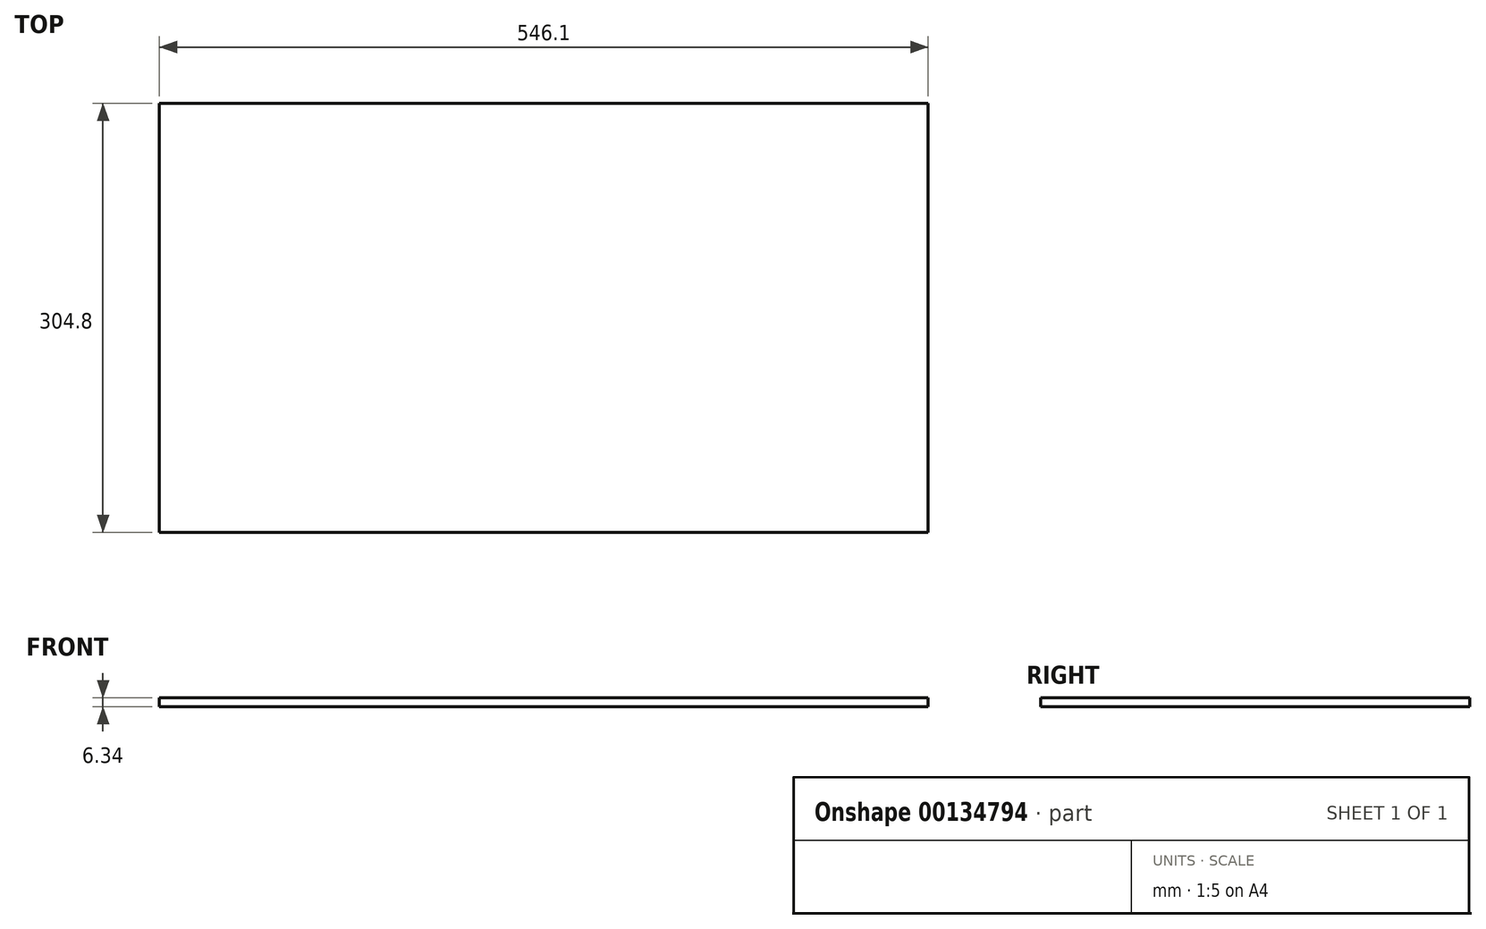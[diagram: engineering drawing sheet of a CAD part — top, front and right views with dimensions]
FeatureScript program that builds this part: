
annotation { "Feature Type Name" : "Feature", "Feature Type Description" : "" }
export const myFeature = defineFeature(function(context is Context, id is Id, definition is map)
    precondition{}
    {
        {
            var Q0;
            Q0=qCreatedBy(makeId("Top.planeOp"),FACE);
            var sketch = newSketch(context, id + "F0", { "sketchPlane" : qUnion([Q0])});
            skLineSegment(sketch, "E0.bottom", {"start": v(273.05, 152.4) * mm, "end": v(-273.05, 152.4) * mm});
            skLineSegment(sketch, "E0.top", {"start": v(273.05, -152.4) * mm, "end": v(-273.05, -152.4) * mm});
            skLineSegment(sketch, "E0.left", {"start": v(273.05, 152.4) * mm, "end": v(273.05, -152.4) * mm});
            skLineSegment(sketch, "E0.right", {"start": v(-273.05, 152.4) * mm, "end": v(-273.05, -152.4) * mm});
            skPoint(sketch, "E0.middle", {"position": v(0, 0) * mm});
            skSolve(sketch);
        }
        {
            var Q0;
            Q0=makeQuery(id+"F0.imprint","IMPRINT",FACE,{"disambiguationData":[TD([[makeQuery(id+"F0.imprint","IMPRINT",EDGE,{"derivedFrom":sQuery(id+"F0.wireOp",EDGE,"E0.bottom")}),1.0]])]});
            extrude(context, id + "F1", {"entities" : qUnion([Q0]), "depth" : 6.35 * mm, "symmetric" : true});
        }
    });
